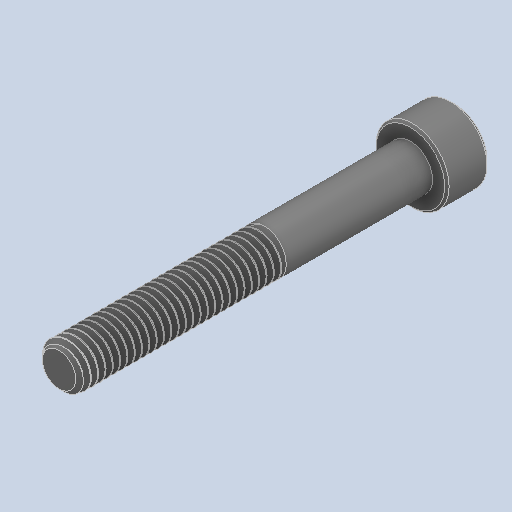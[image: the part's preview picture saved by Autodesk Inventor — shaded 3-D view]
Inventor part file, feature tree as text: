
AUTODESK INVENTOR PART (.ipt)
format: ipt  version: 2024.2 (Build 282272000, 272)  size: 691,712 bytes
history: native  units: in
note: dims shown in document units (in); Inventor stores cm internally (conversion verified against a paired STEP export)
features: chamfer x1
ambient origin geometry x8: Origin, YZ Plane, XZ Plane, XY Plane, X Axis, Y Axis, Z Axis, Center Point
bodies: Solid1 (feature_tree)
feature tree (1):
  chamfer  "Chamfer2"  [1 undecoded]
note: 1 required parameter value undecoded (feature->parameter linkage not recoverable at this tier; creation-order binding heuristic only, values carry confidence <= 0.55)
